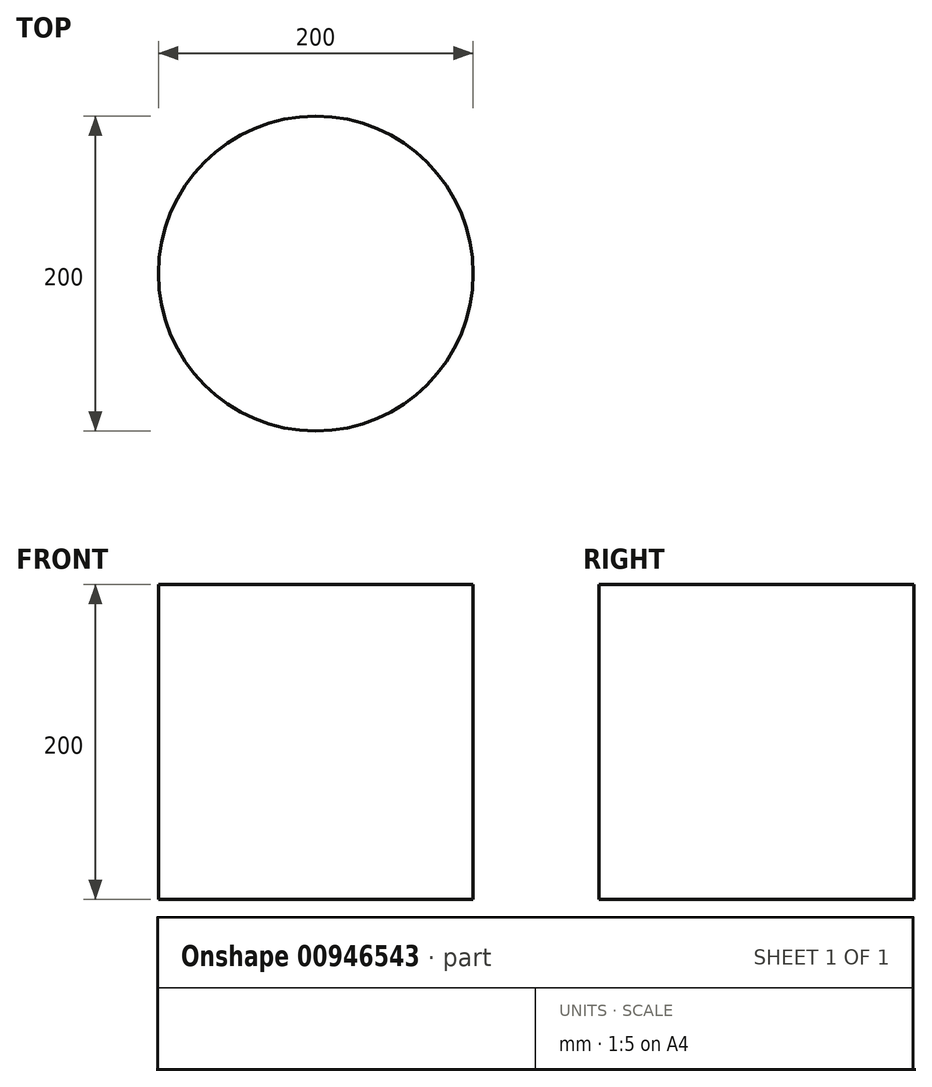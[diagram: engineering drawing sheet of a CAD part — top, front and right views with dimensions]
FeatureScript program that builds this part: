
annotation { "Feature Type Name" : "Feature", "Feature Type Description" : "" }
export const myFeature = defineFeature(function(context is Context, id is Id, definition is map)
    precondition{}
    {
        {
            var Q0;
            Q0=qCreatedBy(makeId("Top.planeOp"),FACE);
            var sketch = newSketch(context, id + "F0", { "sketchPlane" : qUnion([Q0])});
            skCircle(sketch, "E0", {"center": v(0, 0) * mm, "radius": 100 * mm});
            skSolve(sketch);
        }
        {
            var Q0;
            Q0 = qSketchRegion(id + "F0", true);
            extrude(context, id + "F1", {"entities" : qUnion([Q0]), "oppositeDirection" : true, "depth" : 200 * mm, "offsetDistance" : 25 * mm});
        }
    });
